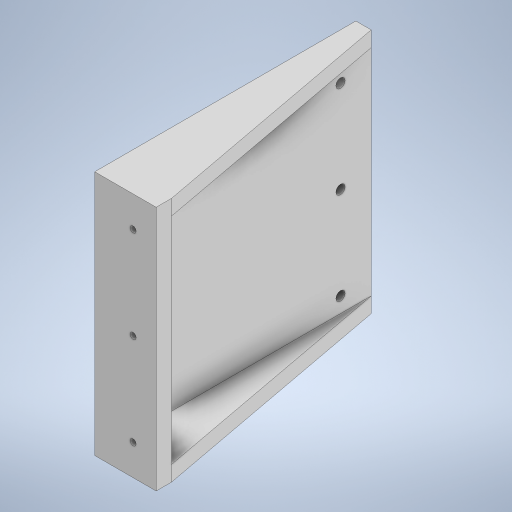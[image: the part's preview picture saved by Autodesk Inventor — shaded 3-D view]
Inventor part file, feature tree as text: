
AUTODESK INVENTOR PART (.ipt)
format: ipt  version: 2023 (Build 270158000, 158)  size: 313,856 bytes
history: native  units: mm
features: extrude x7, sketch x7
ambient origin geometry x8: Origin, YZ Plane, XZ Plane, XY Plane, X Axis, Y Axis, Z Axis, Center Point
bodies: Body1 (feature_tree)
feature tree (14):
  extrude  "Extrusion15"  Depth=160.0mm
  extrude  "Extrusion16"  Depth=170.0mm
  extrude  "Extrusion17"  Depth=10.0mm TaperAngle=0.0deg
  extrude  "Extrusion18"  Depth=10.0mm TaperAngle=0.0deg
  extrude  "Extrusion19"  Depth=4.0mm
  extrude  "Extrusion20"  Depth=4.0mm TaperAngle=0.0deg
  extrude  "Extrusion21"  Depth=4.0mm
  sketch  "Sketch21"  dims[d53=30.0mm d1=160.0mm]
  sketch  "Sketch22"  dims[d55=10.0mm d56=0.0mm d57=170.0mm]
  sketch  "Sketch23"  dims[d58=160.0mm d59=10.0mm d60=0.0mm]
  sketch  "Sketch24"  dims[d61=10.0mm d62=0.0mm d63=10.0mm d64=0.0mm]
  sketch  "Sketch25"  dims[d65=4.0mm d66=4.0mm]
  sketch  "Sketch27"  dims[d67=4.0mm d68=20.0mm d69=0.0mm]
  sketch  "Sketch29"  dims[d70=20.0mm d71=20.0mm d72=80.0mm d73=20.0mm d74=6.0mm d75=6.0mm d76=80.0mm d77=6.0mm d78=20.0mm d79=20.0mm d80=20.0mm d81=20.0mm d82=20.0mm d83=0.0mm d84=6.0mm d85=20.0mm d86=80.0mm d87=6.0mm d88=20.0mm d89=20.0mm d90=6.0mm d91=20.0mm d92=20.0mm d93=10.0mm d94=10.0mm d95=10.0mm d96=10.0mm d97=10.0mm d98=10.0mm d99=4.0mm d100=0.0mm d49=0.5mm d50=0.872665mm d51=0.5mm d52=0.872665mm]
